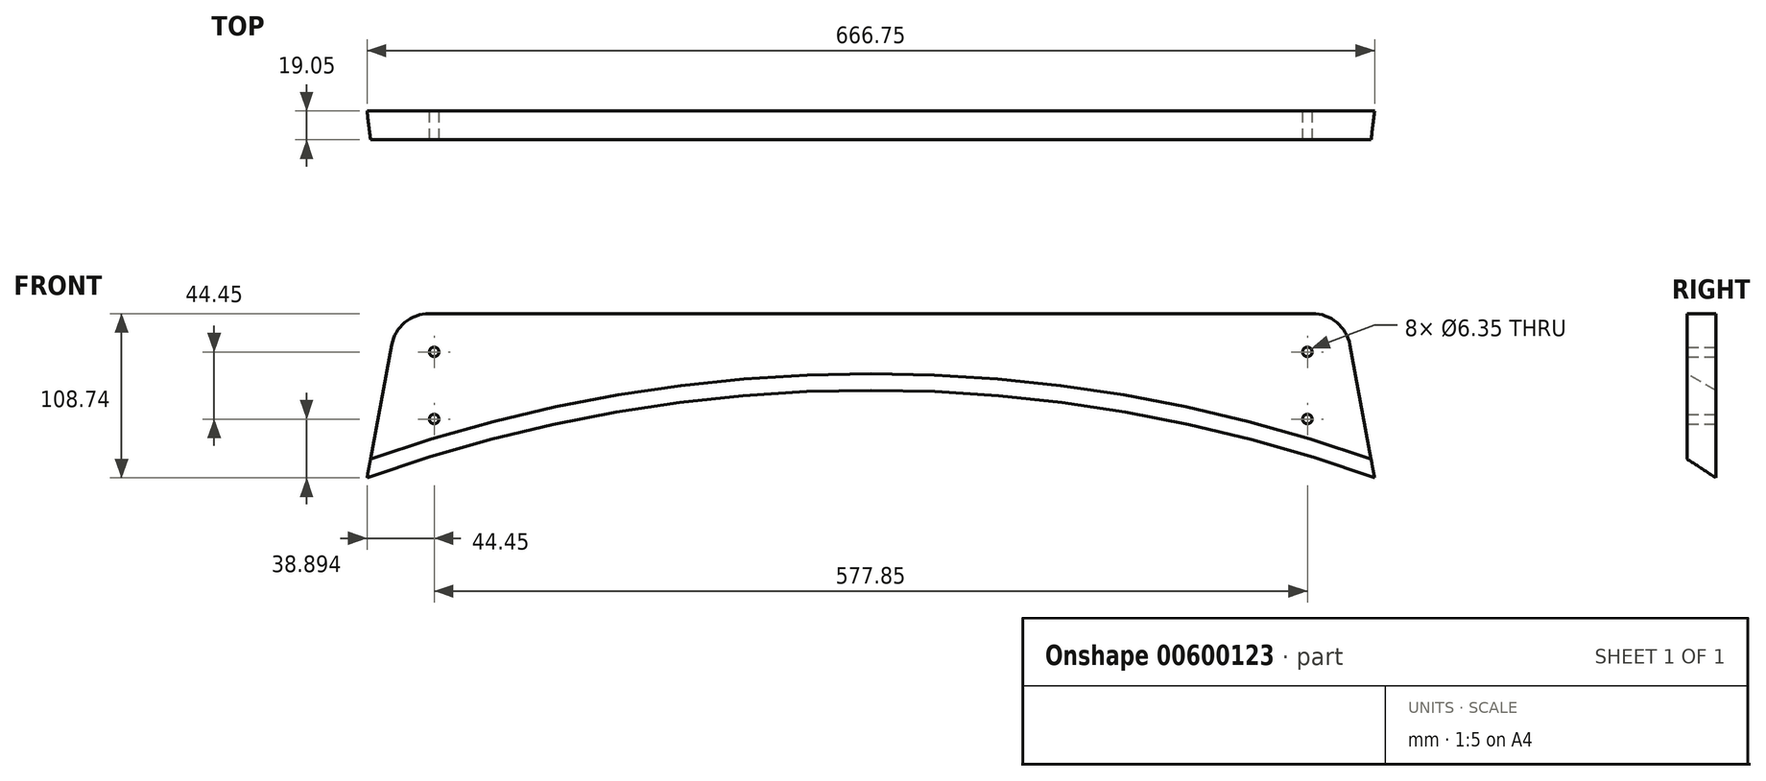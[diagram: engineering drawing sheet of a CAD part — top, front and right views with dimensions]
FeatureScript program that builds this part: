
annotation { "Feature Type Name" : "Feature", "Feature Type Description" : "" }
export const myFeature = defineFeature(function(context is Context, id is Id, definition is map)
    precondition{}
    {
        {
            var Q0;
            Q0=qCreatedBy(makeId("Front.planeOp"),FACE);
            var sketch = newSketch(context, id + "F0", { "sketchPlane" : qUnion([Q0])});
            skLineSegment(sketch, "E0", {"start": v(0, 0) * mm, "end": v(-666.75, 0) * mm});
            skLineSegment(sketch, "E1", {"start": v(-333.38, 0) * mm, "end": v(-333.38, 57.94) * mm, "construction": true});
            skArc(sketch, "E2", {"start": v(0, 0) * mm, "mid": v(-333.37, 57.94) * mm, "end": v(-666.75, 0) * mm, "construction": true});
            skLineSegment(sketch, "E3", {"start": v(-41.28, 108.74) * mm, "end": v(-625.48, 108.74) * mm});
            skArc(sketch, "E4", {"start": v(-625.48, 108.74) * mm, "mid": v(-641.72, 102.87) * mm, "end": v(-650.45, 87.97) * mm});
            skLineSegment(sketch, "E5", {"start": v(-650.45, 87.97) * mm, "end": v(-666.75, 0) * mm});
            skArc(sketch, "E6.MirrorCS", {"start": v(-41.28, 108.74) * mm, "mid": v(-25.03, 102.87) * mm, "end": v(-16.3, 87.97) * mm});
            skLineSegment(sketch, "E7.MirrorCS", {"start": v(-16.3, 87.97) * mm, "end": v(0, 0) * mm});
            skLineSegment(sketch, "E8.bottom", {"start": v(-622.3, 83.34) * mm, "end": v(-44.45, 83.34) * mm, "construction": true});
            skLineSegment(sketch, "E8.top", {"start": v(-622.3, 38.9) * mm, "end": v(-44.45, 38.9) * mm, "construction": true});
            skLineSegment(sketch, "E8.left", {"start": v(-622.3, 83.34) * mm, "end": v(-622.3, 38.9) * mm, "construction": true});
            skLineSegment(sketch, "E8.right", {"start": v(-44.45, 83.34) * mm, "end": v(-44.45, 38.9) * mm, "construction": true});
            skLineSegment(sketch, "E9", {"start": v(-333.38, 83.34) * mm, "end": v(-333.38, 57.94) * mm, "construction": true});
            skCircle(sketch, "E10", {"center": v(-622.3, 38.9) * mm, "radius": 3.18 * mm});
            skCircle(sketch, "E11", {"center": v(-622.3, 83.34) * mm, "radius": 3.18 * mm});
            skCircle(sketch, "E12", {"center": v(-44.45, 83.34) * mm, "radius": 3.18 * mm});
            skCircle(sketch, "E13", {"center": v(-44.45, 38.9) * mm, "radius": 3.18 * mm});
            skSolve(sketch);
        }
        {
            var Q0;
            Q0 = qSketchRegion(id + "F0", true);
            extrude(context, id + "F1", {"entities" : qUnion([Q0]), "depth" : 19.05 * mm, "offsetDistance" : 25.4 * mm});
        }
        {
            var Q0;
            Q0=sQuery(id+"F0.wireOp",VERTEX,"E1.end");
            var Q1;
            Q1=qCreatedBy(makeId("Right.planeOp"),FACE);
            cPlane(context, id + "F2", {"entities" : qUnion([Q0, Q1]), "cplaneType" : CPlaneType.PLANE_POINT, "offset" : 25.4 * mm, "width" : 152.4 * mm, "height" : 152.4 * mm});
        }
        {
            var Q0;
            Q0=qCreatedBy(id+"F2.planeOp",FACE);
            var sketch = newSketch(context, id + "F3", { "sketchPlane" : qUnion([Q0])});
            skLineSegment(sketch, "E14", {"start": v(-50.8, 87.27) * mm, "end": v(50.8, 28.61) * mm});
            skLineSegment(sketch, "E15", {"start": v(-50.8, 87.27) * mm, "end": v(-50.8, -930.05) * mm});
            skLineSegment(sketch, "E16", {"start": v(-50.8, -930.05) * mm, "end": v(50.8, -930.05) * mm});
            skLineSegment(sketch, "E17", {"start": v(50.8, -930.05) * mm, "end": v(50.8, 28.61) * mm});
            skLineSegment(sketch, "E18", {"start": v(0, 57.94) * mm, "end": v(64.86, 57.94) * mm, "construction": true});
            skSolve(sketch);
        }
        {
            var Q0;
            Q0 = qSketchRegion(id + "F3", true);
            var Q1;
            Q1=sQuery(id+"F3.wireOp",EDGE,"E16");
            revolve(context, id + "F4", {"operationType" : NewBodyOperationType.REMOVE, "entities" : qUnion([Q0]), "axis" : qUnion([Q1]), "revolveType" : RevolveType.FULL, "oppositeDirection" : true});
        }
    });
